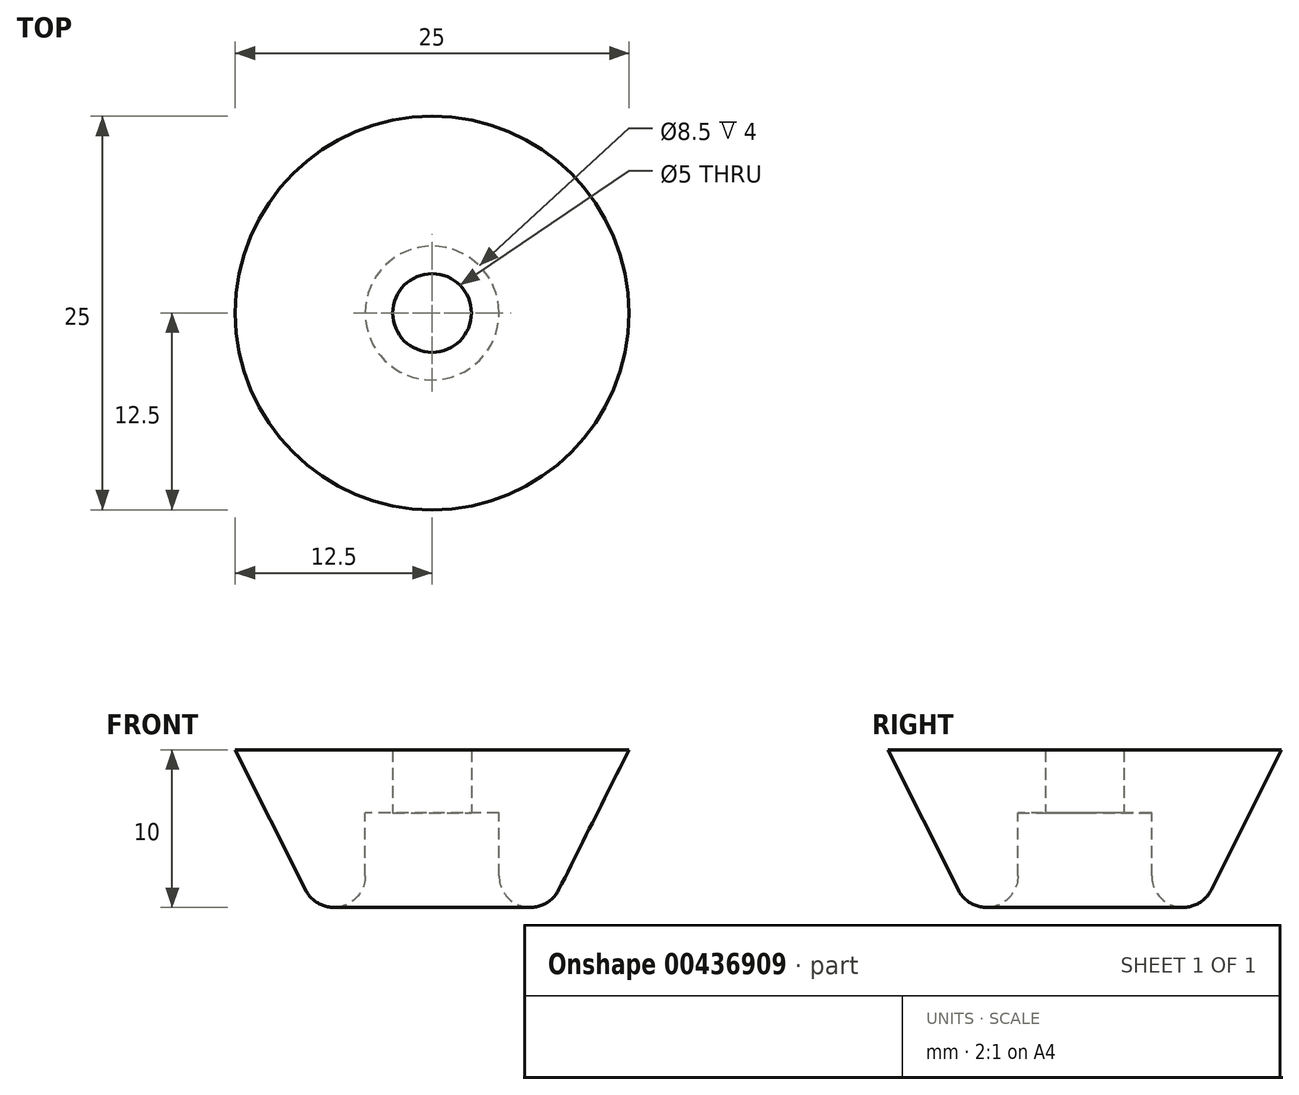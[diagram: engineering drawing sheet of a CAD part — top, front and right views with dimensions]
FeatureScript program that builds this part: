
annotation { "Feature Type Name" : "Feature", "Feature Type Description" : "" }
export const myFeature = defineFeature(function(context is Context, id is Id, definition is map)
    precondition{}
    {
        {
            var Q0;
            Q0=qCreatedBy(makeId("Front.planeOp"),FACE);
            var sketch = newSketch(context, id + "F0", { "sketchPlane" : qUnion([Q0])});
            skLineSegment(sketch, "E0", {"start": v(0, 0) * mm, "end": v(0, -4) * mm});
            skLineSegment(sketch, "E1", {"start": v(0, -4) * mm, "end": v(4.25, -4) * mm});
            skLineSegment(sketch, "E2", {"start": v(4.25, -4) * mm, "end": v(4.25, -8) * mm});
            skLineSegment(sketch, "E3", {"start": v(12.5, 0) * mm, "end": v(0, 0) * mm});
            skLineSegment(sketch, "E4", {"start": v(12.5, 0) * mm, "end": v(8.04, -8.9) * mm});
            skPoint(sketch, "E5.visualSharp", {"position": v(4.25, -16.45) * mm});
            skArc(sketch, "E5.filletArc", {"start": v(4.25, -8) * mm, "mid": v(5.79, -9.95) * mm, "end": v(8.04, -8.9) * mm});
            skSolve(sketch);
        }
        {
            var Q0;
            Q0 = qSketchRegion(id + "F0", true);
            var Q1;
            Q1=sQuery(id+"F0.wireOp",EDGE,"E0");
            revolve(context, id + "F1", {"entities" : qUnion([Q0]), "axis" : qUnion([Q1]), "revolveType" : RevolveType.FULL});
        }
        {
            var Q0;
            Q0=makeQuery(id+"F1.opRevolve","SWEPT_FACE",FACE,{"disambiguationData":[OSD([sQuery(id+"F0.wireOp",EDGE,"E1")])]});
            var sketch = newSketch(context, id + "F2", { "sketchPlane" : qUnion([Q0])});
            skCircle(sketch, "E6", {"center": v(0, 0) * mm, "radius": 2.5 * mm});
            skSolve(sketch);
        }
        {
            var Q0;
            Q0 = qSketchRegion(id + "F2", true);
            extrude(context, id + "F3", {"entities" : qUnion([Q0]), "operationType" : NewBodyOperationType.REMOVE, "endBound" : BoundingType.THROUGH_ALL, "oppositeDirection" : true, "depth" : 25 * mm});
        }
    });
